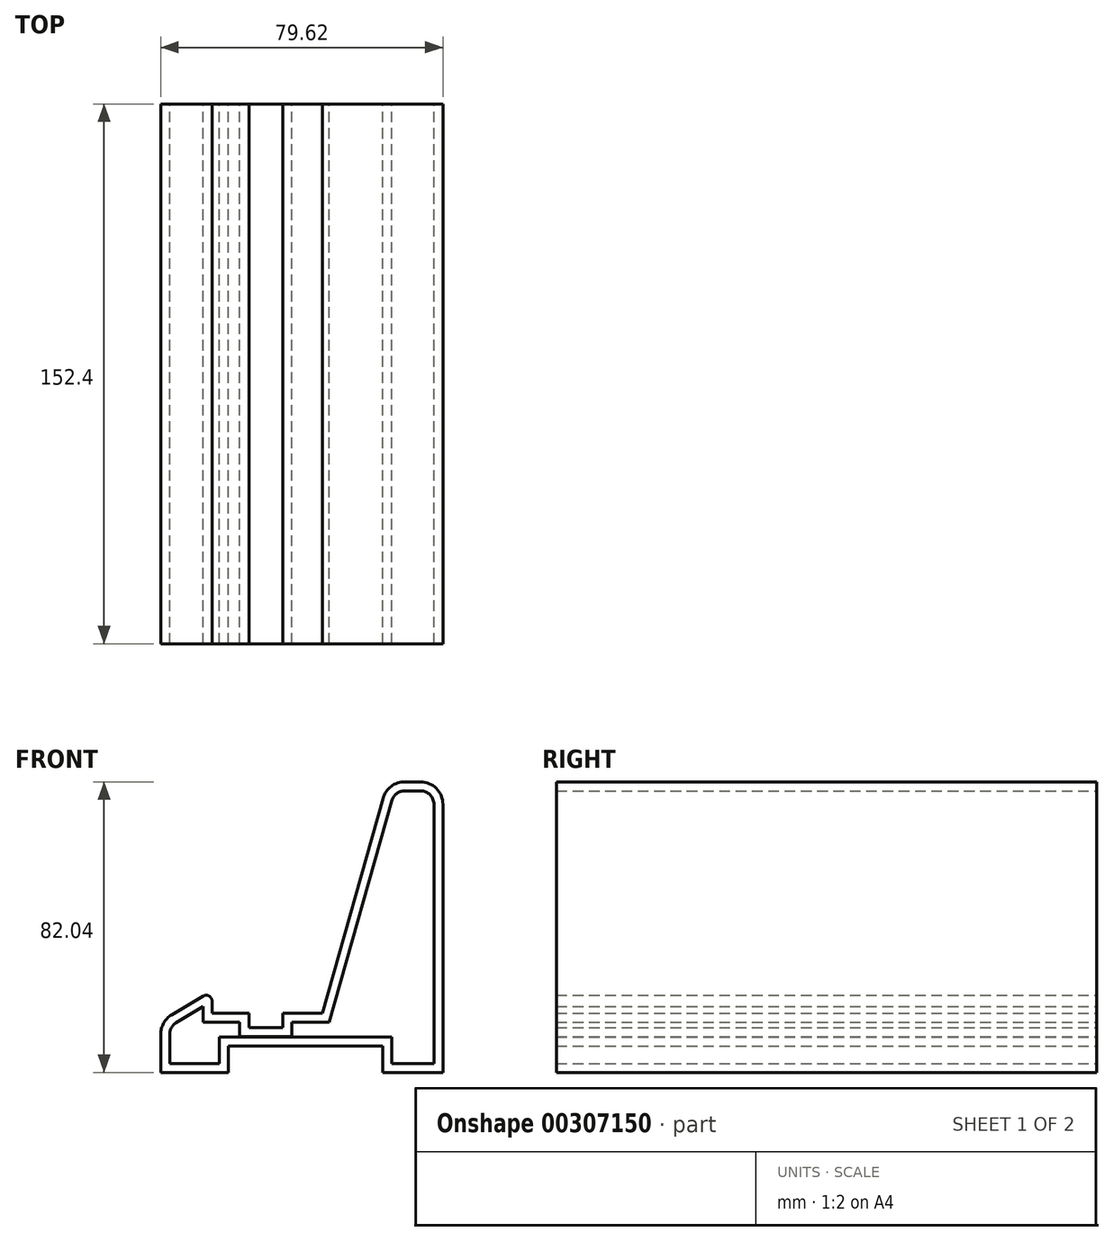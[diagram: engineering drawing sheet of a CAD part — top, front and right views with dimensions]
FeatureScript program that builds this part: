
annotation { "Feature Type Name" : "Feature", "Feature Type Description" : "" }
export const myFeature = defineFeature(function(context is Context, id is Id, definition is map)
    precondition{}
    {
        {
            var Q0;
            Q0=qCreatedBy(makeId("Front.planeOp"),FACE);
            var sketch = newSketch(context, id + "F0", { "sketchPlane" : qUnion([Q0])});
            skLineSegment(sketch, "E0", {"start": v(-48.23, -10.7) * mm, "end": v(-37.83, -10.7) * mm});
            skLineSegment(sketch, "E1", {"start": v(-17.1, -10.7) * mm, "end": v(0.04, 50.03) * mm});
            skLineSegment(sketch, "E2", {"start": v(-48.23, -10.7) * mm, "end": v(-48.23, -7.24) * mm});
            skLineSegment(sketch, "E3", {"start": v(6.15, 54.66) * mm, "end": v(10.58, 54.66) * mm});
            skLineSegment(sketch, "E4", {"start": v(16.93, 48.3) * mm, "end": v(16.93, -27.38) * mm});
            skLineSegment(sketch, "E5", {"start": v(16.93, -27.38) * mm, "end": v(0, -27.38) * mm});
            skLineSegment(sketch, "E6", {"start": v(-62.69, -27.38) * mm, "end": v(-62.69, -16.58) * mm});
            skLineSegment(sketch, "E7", {"start": v(-59.6, -11.12) * mm, "end": v(-50.7, -5.83) * mm});
            skLineSegment(sketch, "E8", {"start": v(-62.69, -27.38) * mm, "end": v(-43.6, -27.38) * mm});
            skLineSegment(sketch, "E9.trimOffspring", {"start": v(-43.6, -27.38) * mm, "end": v(-62.69, -27.38) * mm});
            skPoint(sketch, "E10.visualSharp", {"position": v(-48.23, -4.35) * mm});
            skArc(sketch, "E10.filletArc", {"start": v(-48.23, -7.24) * mm, "mid": v(-49.06, -5.81) * mm, "end": v(-50.7, -5.83) * mm});
            skPoint(sketch, "E11.visualSharp", {"position": v(16.93, 54.66) * mm});
            skArc(sketch, "E11.filletArc", {"start": v(16.93, 48.3) * mm, "mid": v(15.07, 52.8) * mm, "end": v(10.58, 54.66) * mm});
            skPoint(sketch, "E12.visualSharp", {"position": v(1.34, 54.66) * mm});
            skArc(sketch, "E12.filletArc", {"start": v(6.15, 54.66) * mm, "mid": v(2.32, 53.37) * mm, "end": v(0.04, 50.03) * mm});
            skPoint(sketch, "E13.visualSharp", {"position": v(-62.69, -12.97) * mm});
            skArc(sketch, "E13.filletArc", {"start": v(-59.6, -11.12) * mm, "mid": v(-61.86, -13.44) * mm, "end": v(-62.69, -16.58) * mm});
            skLineSegment(sketch, "E14", {"start": v(-28.22, -10.7) * mm, "end": v(-28.22, -14.7) * mm});
            skLineSegment(sketch, "E15", {"start": v(-28.22, -14.7) * mm, "end": v(-37.83, -14.7) * mm});
            skLineSegment(sketch, "E16", {"start": v(-37.83, -14.7) * mm, "end": v(-37.83, -10.7) * mm});
            skLineSegment(sketch, "E17.trimOffspring", {"start": v(-28.22, -10.7) * mm, "end": v(-17.1, -10.7) * mm});
            skLineSegment(sketch, "E18", {"start": v(0, -27.38) * mm, "end": v(0, 0) * mm});
            skLineSegment(sketch, "E19", {"start": v(-43.6, -27.38) * mm, "end": v(-43.6, -20) * mm});
            skLineSegment(sketch, "E20", {"start": v(-43.6, -20) * mm, "end": v(0, -20) * mm});
            skLineSegment(sketch, "E21", {"start": v(0, -20) * mm, "end": v(0, -27.38) * mm});
            skSolve(sketch);
        }
        {
            var Q0;
            Q0=makeQuery(id+"F0.imprint","IMPRINT",FACE,{"disambiguationData":[TD([[makeQuery(id+"F0.imprint","IMPRINT",EDGE,{"derivedFrom":sQuery(id+"F0.wireOp",EDGE,"E0")}),-1.0]])]});
            extrude(context, id + "F1", {"entities" : qUnion([Q0]), "depth" : 152.4 * mm});
        }
        {
            var Q0;
            Q0=makeQuery(id+"F1.opExtrude","CAP_FACE",FACE,{"disambiguationData":[OSD([sQuery(id+"F0.wireOp",EDGE,"E0"),sQuery(id+"F0.wireOp",EDGE,"E1"),sQuery(id+"F0.wireOp",EDGE,"E2"),sQuery(id+"F0.wireOp",EDGE,"E3"),sQuery(id+"F0.wireOp",EDGE,"E4"),sQuery(id+"F0.wireOp",EDGE,"E5"),sQuery(id+"F0.wireOp",EDGE,"E6"),sQuery(id+"F0.wireOp",EDGE,"E7"),sQuery(id+"F0.wireOp",EDGE,"xid2QMFl-hO0d-wp1L-Nn0s-pwgOk6QZDywa"),sQuery(id+"F0.wireOp",EDGE,"KuW0eG9z-wIUD-hqS5-V8Qh-E1k4Mr5AA6uD"),sQuery(id+"F0.wireOp",EDGE,"Cs7n8h3h-nPpJ-F1FO-fnAx-N4HORvhUJ9CG"),sQuery(id+"F0.wireOp",EDGE,"D7dDi9Du-MR0k-yKEk-S20u-8SZaRIVXlcED"),sQuery(id+"F0.wireOp",EDGE,"JGvh5d2B-4pgD-T76B-y9iA-Obl0XFSilnUt"),sQuery(id+"F0.wireOp",EDGE,"ZoV2flYp-ep4Q-YLVT-Wv5x-7XDLpLIdwywF"),sQuery(id+"F0.wireOp",EDGE,"jGNN14KM-oJjJ-6neP-icxM-Aa9whrPcKXbL"),sQuery(id+"F0.wireOp",EDGE,"E9.trimOffspring"),sQuery(id+"F0.wireOp",EDGE,"E10.filletArc")])],"isStart":false});
            var Q1;
            Q1=makeQuery(id+"F1.opExtrude","CAP_FACE",FACE,{"disambiguationData":[OSD([sQuery(id+"F0.wireOp",EDGE,"E0"),sQuery(id+"F0.wireOp",EDGE,"E1"),sQuery(id+"F0.wireOp",EDGE,"E2"),sQuery(id+"F0.wireOp",EDGE,"E3"),sQuery(id+"F0.wireOp",EDGE,"E4"),sQuery(id+"F0.wireOp",EDGE,"E5"),sQuery(id+"F0.wireOp",EDGE,"E6"),sQuery(id+"F0.wireOp",EDGE,"E7"),sQuery(id+"F0.wireOp",EDGE,"xid2QMFl-hO0d-wp1L-Nn0s-pwgOk6QZDywa"),sQuery(id+"F0.wireOp",EDGE,"KuW0eG9z-wIUD-hqS5-V8Qh-E1k4Mr5AA6uD"),sQuery(id+"F0.wireOp",EDGE,"Cs7n8h3h-nPpJ-F1FO-fnAx-N4HORvhUJ9CG"),sQuery(id+"F0.wireOp",EDGE,"D7dDi9Du-MR0k-yKEk-S20u-8SZaRIVXlcED"),sQuery(id+"F0.wireOp",EDGE,"JGvh5d2B-4pgD-T76B-y9iA-Obl0XFSilnUt"),sQuery(id+"F0.wireOp",EDGE,"ZoV2flYp-ep4Q-YLVT-Wv5x-7XDLpLIdwywF"),sQuery(id+"F0.wireOp",EDGE,"jGNN14KM-oJjJ-6neP-icxM-Aa9whrPcKXbL"),sQuery(id+"F0.wireOp",EDGE,"E9.trimOffspring"),sQuery(id+"F0.wireOp",EDGE,"E10.filletArc")])],"isStart":true});
            shell(context, id + "F2", {"entities" : qUnion([Q0, Q1]), "thickness" : 2.54 * mm});
        }
    });
